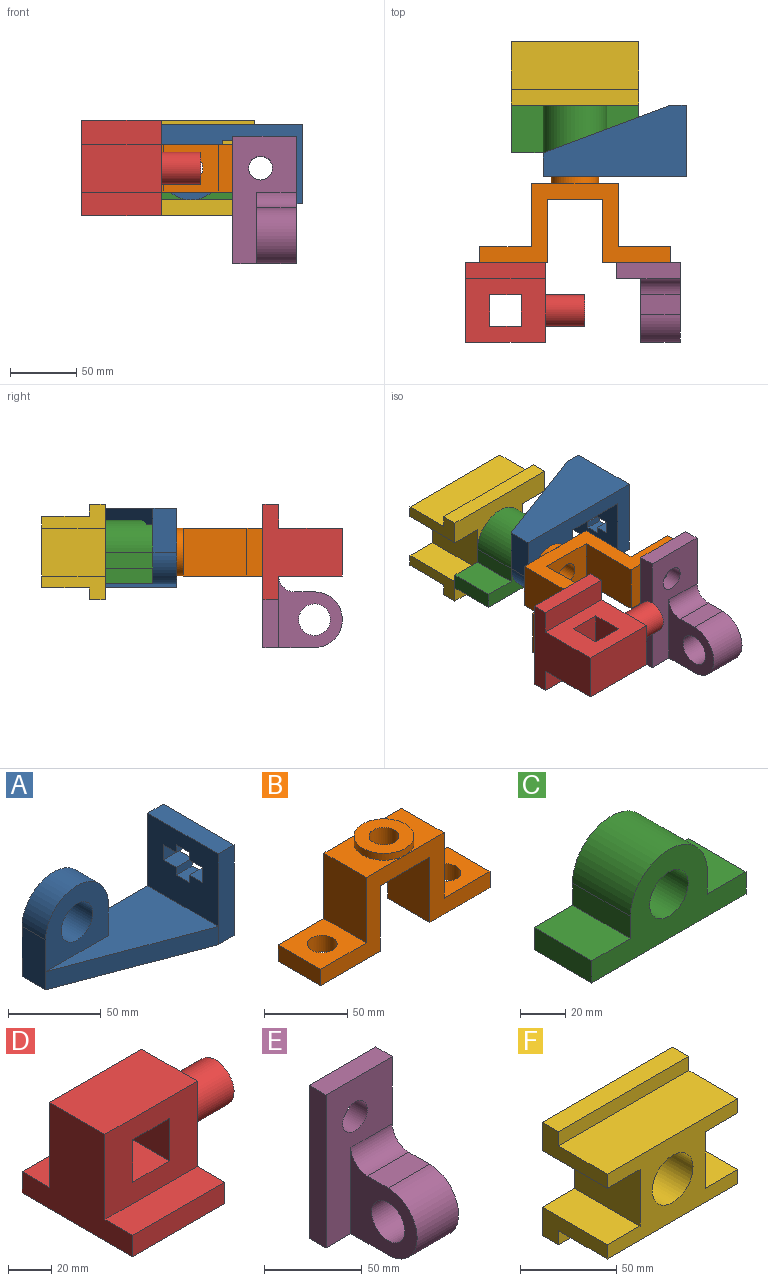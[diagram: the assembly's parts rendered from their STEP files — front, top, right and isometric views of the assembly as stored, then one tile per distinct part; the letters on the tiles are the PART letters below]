
ASSEMBLY  parts=6 mates=5
PART A: 25 faces, bbox 108x54x60 mm
  f0: plane 108x60mm, normal (0,1,0), area 3332.4mm2, adj f1,f2,f3,f4,f5,f8,f9,f23
  f1: plane 33x18mm, normal (-1,0,0), area 594mm2, adj f0,f6,f8,f22,f23
  f2: plane 21x18mm, normal (1,0,0), area 378mm2, adj f0,f3,f22,f23
  f3: plane 96x54mm, normal (0,0,1), area 2592mm2, adj f0,f2,f5,f6,f22
  f4: plane 60x54mm, normal (1,0,0), area 2840mm2, adj f0,f7,f8,f9,f10,f11,f12,f13
  f5: plane 54x48mm, normal (-1,0,0), area 2192mm2, adj f0,f3,f7,f9,f10,f11,f12,f13
  f6: plane 96x36mm, normal (-0.35,-0.94,0), area 1230.3mm2, adj f1,f3,f7,f8
  f7: plane 60x12mm, normal (0,-1,0), area 720mm2, adj f4,f5,f6,f8,f9
  f8: plane 108x54mm, normal (0,0,-1), area 4104mm2, adj f0,f1,f4,f6,f7
  f9: plane 54x12mm, normal (0,0,1), area 648mm2, adj f0,f4,f5,f7
  f10: plane 12x10mm, normal (0,0,-1), area 120mm2, adj f4,f5,f11,f21
  f11: plane 12x5mm, normal (0,1,0), area 60mm2, adj f4,f5,f10,f12
  f12: plane 12x10mm, normal (0,0,-1), area 120mm2, adj f4,f5,f11,f13
  f13: plane 12x10mm, normal (0,1,0), area 120mm2, adj f4,f5,f12,f14
  f14: plane 12x10mm, normal (0,0,1), area 120mm2, adj f4,f5,f13,f15
  f15: plane 12x5mm, normal (0,1,0), area 60mm2, adj f4,f5,f14,f16
  f16: plane 12x10mm, normal (0,0,1), area 120mm2, adj f4,f5,f15,f17
  f17: plane 12x5mm, normal (0,-1,0), area 60mm2, adj f4,f5,f16,f18
  f18: plane 12x10mm, normal (0,0,1), area 120mm2, adj f4,f5,f17,f19
  f19: plane 12x10mm, normal (0,-1,0), area 120mm2, adj f4,f5,f18,f20
  f20: plane 12x10mm, normal (0,0,-1), area 120mm2, adj f4,f5,f19,f21
  f21: plane 12x5mm, normal (0,-1,0), area 60mm2, adj f4,f5,f10,f20
  f22: plane 48x45mm, normal (0,-1,0), area 1460.4mm2, adj f1,f2,f3,f23,f24
  f23: cylinder r=24mm len=48mm, axis (0,-1,0), area 1357.2mm2, adj f0,f1,f2,f22
  f24: cylinder r=12mm len=24mm, axis (0,-1,0), area 1357.2mm2, adj f0,f22
PART B: 20 faces, bbox 144x36x65 mm
  f0: plane 36x33mm, normal (0,0,1), area 679.1mm2, adj f1,f3,f10,f18
  f1: plane 144x60mm, normal (0,1,0), area 2880mm2, adj f0,f2,f5,f6,f7,f8,f9,f10
  f2: plane 48x36mm, normal (-1,0,0), area 1728mm2, adj f1,f3,f7,f11
  f3: plane 144x60mm, normal (0,-1,0), area 2880mm2, adj f0,f2,f5,f6,f7,f8,f9,f10
  f4: cylinder r=9mm len=18mm, axis (0,0,-1), area 678.6mm2, adj f6,f7
  f5: plane 36x12mm, normal (1,0,0), area 432mm2, adj f1,f3,f6,f7
  f6: plane 39x36mm, normal (0,0,1), area 1149.5mm2, adj f1,f3,f4,f5,f8
  f7: plane 51x36mm, normal (0,0,-1), area 1581.5mm2, adj f1,f2,f3,f4,f5
  f8: plane 48x36mm, normal (1,0,0), area 1728mm2, adj f1,f3,f6,f9
  f9: plane 36x33mm, normal (0,0,1), area 679.1mm2, adj f1,f3,f8,f18
  f10: plane 48x36mm, normal (-1,0,0), area 1728mm2, adj f0,f1,f3,f15
  f11: plane 42x36mm, normal (0,0,-1), area 1257.5mm2, adj f1,f2,f3,f12,f17
  f12: plane 48x36mm, normal (1,0,0), area 1728mm2, adj f1,f3,f11,f16
  f13: plane 36x12mm, normal (-1,0,0), area 432mm2, adj f1,f3,f15,f16
  f14: cylinder r=9mm len=18mm, axis (0,0,-1), area 678.6mm2, adj f15,f16
  f15: plane 39x36mm, normal (0,0,1), area 1149.5mm2, adj f1,f3,f10,f13,f14
  f16: plane 51x36mm, normal (0,0,-1), area 1581.5mm2, adj f1,f3,f12,f13,f14
  f17: cylinder r=9mm len=18mm, axis (0,0,-1), area 961.3mm2, adj f11,f19
  f18: cylinder r=18mm len=36mm, axis (0,0,-1), area 565.5mm2, adj f0,f9,f19
  f19: plane 36x36mm, normal (0,0,1), area 763.4mm2, adj f17,f18
PART C: 11 faces, bbox 96x36x48 mm
  f0: plane 96x48mm, normal (0,1,0), area 2180.4mm2, adj f2,f3,f4,f5,f6,f7,f8,f9
  f1: plane 96x48mm, normal (0,-1,0), area 2180.4mm2, adj f2,f3,f4,f5,f6,f7,f8,f9
  f2: plane 36x12mm, normal (-1,0,0), area 432mm2, adj f0,f1,f7,f9
  f3: plane 36x12mm, normal (1,0,0), area 432mm2, adj f0,f1,f4,f9
  f4: plane 36x24mm, normal (0,0,1), area 864mm2, adj f0,f1,f3,f5
  f5: plane 36x12mm, normal (1,0,0), area 432mm2, adj f0,f1,f4,f8
  f6: plane 36x12mm, normal (-1,0,0), area 432mm2, adj f0,f1,f7,f8
  f7: plane 36x24mm, normal (0,0,1), area 864mm2, adj f0,f1,f2,f6
  f8: plane 96x36mm, normal (0,0,-1), area 3456mm2, adj f0,f1,f5,f6
  f9: cylinder r=24mm len=48mm, axis (0,-1,0), area 2714.3mm2, adj f0,f1,f2,f3
  f10: cylinder r=12mm len=36mm, axis (0,-1,0), area 2714.3mm2, adj f0,f1
PART D: 16 faces, bbox 90x72x60 mm
  f0: plane 60x48mm, normal (0,-1,0), area 2304mm2, adj f4,f6,f7,f9,f10,f11,f12,f13
  f1: plane 60x48mm, normal (0,1,0), area 2304mm2, adj f2,f4,f6,f9,f10,f11,f12,f13
  f2: plane 60x18mm, normal (0,0,1), area 1080mm2, adj f1,f3,f4,f6
  f3: plane 60x12mm, normal (0,1,0), area 720mm2, adj f2,f4,f6,f8
  f4: plane 72x60mm, normal (-1,0,0), area 2592mm2, adj f0,f1,f2,f3,f5,f7,f8,f9
  f5: plane 60x12mm, normal (0,-1,0), area 720mm2, adj f4,f6,f7,f8
  f6: plane 72x60mm, normal (1,0,0), area 2139.6mm2, adj f0,f1,f2,f3,f5,f7,f8,f9
  f7: plane 60x18mm, normal (0,0,1), area 1080mm2, adj f0,f4,f5,f6
  f8: plane 72x60mm, normal (0,0,-1), area 4320mm2, adj f3,f4,f5,f6
  f9: plane 60x36mm, normal (0,0,1), area 2160mm2, adj f0,f1,f4,f6
  f10: plane 36x24mm, normal (1,0,0), area 864mm2, adj f0,f1,f11,f13
  f11: plane 36x24mm, normal (0,0,1), area 864mm2, adj f0,f1,f10,f12
  f12: plane 36x24mm, normal (-1,0,0), area 864mm2, adj f0,f1,f11,f13
  f13: plane 36x24mm, normal (0,0,-1), area 864mm2, adj f0,f1,f10,f12
  f14: cylinder r=12mm len=30mm, axis (-1,0,0), area 2261.9mm2, adj f6,f15
  f15: plane 24x24mm, normal (1,0,0), area 452.4mm2, adj f14
PART E: 12 faces, bbox 48x60x96 mm
  f0: plane 96x60mm, normal (1,0,0), area 2557.2mm2, adj f2,f3,f5,f6,f7,f8,f9,f11
  f1: plane 54x48mm, normal (-1,0,0), area 1405.2mm2, adj f2,f6,f7,f8,f9,f11
  f2: plane 96x48mm, normal (0,-1,0), area 2733.5mm2, adj f0,f1,f4,f5,f6,f10,f11
  f3: plane 96x48mm, normal (0,1,0), area 4353.5mm2, adj f0,f4,f5,f6,f10
  f4: plane 96x12mm, normal (-1,0,0), area 1152mm2, adj f2,f3,f5,f6
  f5: plane 48x12mm, normal (0,0,1), area 576mm2, adj f0,f2,f3,f4
  f6: plane 48x39mm, normal (0,0,-1), area 1386mm2, adj f0,f1,f2,f3,f4,f8
  f7: plane 30x15mm, normal (0,0,1), area 450mm2, adj f0,f1,f8,f11
  f8: cylinder r=21mm len=42mm, axis (-1,0,0), area 1979.2mm2, adj f0,f1,f6,f7
  f9: cylinder r=12mm len=30mm, axis (-1,0,0), area 2261.9mm2, adj f0,f1
  f10: cylinder r=9mm len=18mm, axis (0,-1,0), area 678.6mm2, adj f2,f3
  f11: cylinder r=12mm len=30mm, axis (-1,0,0), area 565.5mm2, adj f0,f1,f2,f7
PART F: 19 faces, bbox 96x48x72 mm
  f0: plane 48x24mm, normal (0,0,1), area 1152mm2, adj f2,f4,f8,f9
  f1: plane 96x9mm, normal (0,-1,0), area 864mm2, adj f3,f4,f6,f7
  f2: plane 96x72mm, normal (0,1,0), area 4477.1mm2, adj f0,f3,f4,f5,f6,f9,f10,f11
  f3: plane 48x18mm, normal (-1,0,0), area 540mm2, adj f1,f2,f5,f6,f7,f8
  f4: plane 48x18mm, normal (1,0,0), area 540mm2, adj f0,f1,f2,f6,f7,f8
  f5: plane 48x24mm, normal (0,0,1), area 1152mm2, adj f2,f3,f8,f10
  f6: plane 96x12mm, normal (0,0,-1), area 1152mm2, adj f1,f2,f3,f4
  f7: plane 96x36mm, normal (0,0,-1), area 3456mm2, adj f1,f3,f4,f8
  f8: plane 96x54mm, normal (0,-1,0), area 2749.1mm2, adj f0,f3,f4,f5,f7,f9,f10,f11
  f9: plane 48x36mm, normal (1,0,0), area 1728mm2, adj f0,f2,f8,f15
  f10: plane 48x36mm, normal (-1,0,0), area 1728mm2, adj f2,f5,f8,f11
  f11: plane 48x24mm, normal (0,0,-1), area 1152mm2, adj f2,f8,f10,f12
  f12: plane 48x18mm, normal (-1,0,0), area 540mm2, adj f2,f8,f11,f14,f16,f17
  f13: plane 48x18mm, normal (1,0,0), area 540mm2, adj f2,f8,f14,f15,f16,f17
  f14: plane 96x36mm, normal (0,0,1), area 3456mm2, adj f8,f12,f13,f16
  f15: plane 48x24mm, normal (0,0,-1), area 1152mm2, adj f2,f8,f9,f13
  f16: plane 96x9mm, normal (0,-1,0), area 864mm2, adj f12,f13,f14,f17
  f17: plane 96x12mm, normal (0,0,1), area 1152mm2, adj f2,f12,f13,f16
  f18: cylinder r=15mm len=48mm, axis (0,-1,0), area 4523.9mm2, adj f2,f8
PLACE A rot(axis=(1,0,0),180deg) t=(29.02,90.74,25.78)mm
PLACE B rot(axis=(-1,0,0),90deg) t=(-48.98,-1.26,-7.22)mm
PLACE C t=(-48.98,99.74,-31.22)mm
PLACE D rot(axis=(1,0,0),90deg) t=(-101.48,-1.26,-7.22)mm
PLACE E t=(6.52,-7.26,-79.22)mm
PLACE F rot(axis=(1,0,0),180deg) t=(-48.98,123.74,28.78)mm
MATE planar E.f10 <-> B.f4  axis (0,1,0) through (3.52,-1.26,-7.22)mm
MATE planar D.f8 <-> B.f14  axis (0,1,0) through (-101.48,-1.26,-7.22)mm
MATE planar B.f18 <-> A.f23  axis (0,1,0) through (-48.98,63.74,-7.22)mm
MATE planar F.f18 <-> C.f10  axis (0,-1,0) through (-48.98,117.74,-7.22)mm
MATE planar A.f23 <-> C.f9  axis (0,1,0) through (-48.98,81.74,-7.22)mm
